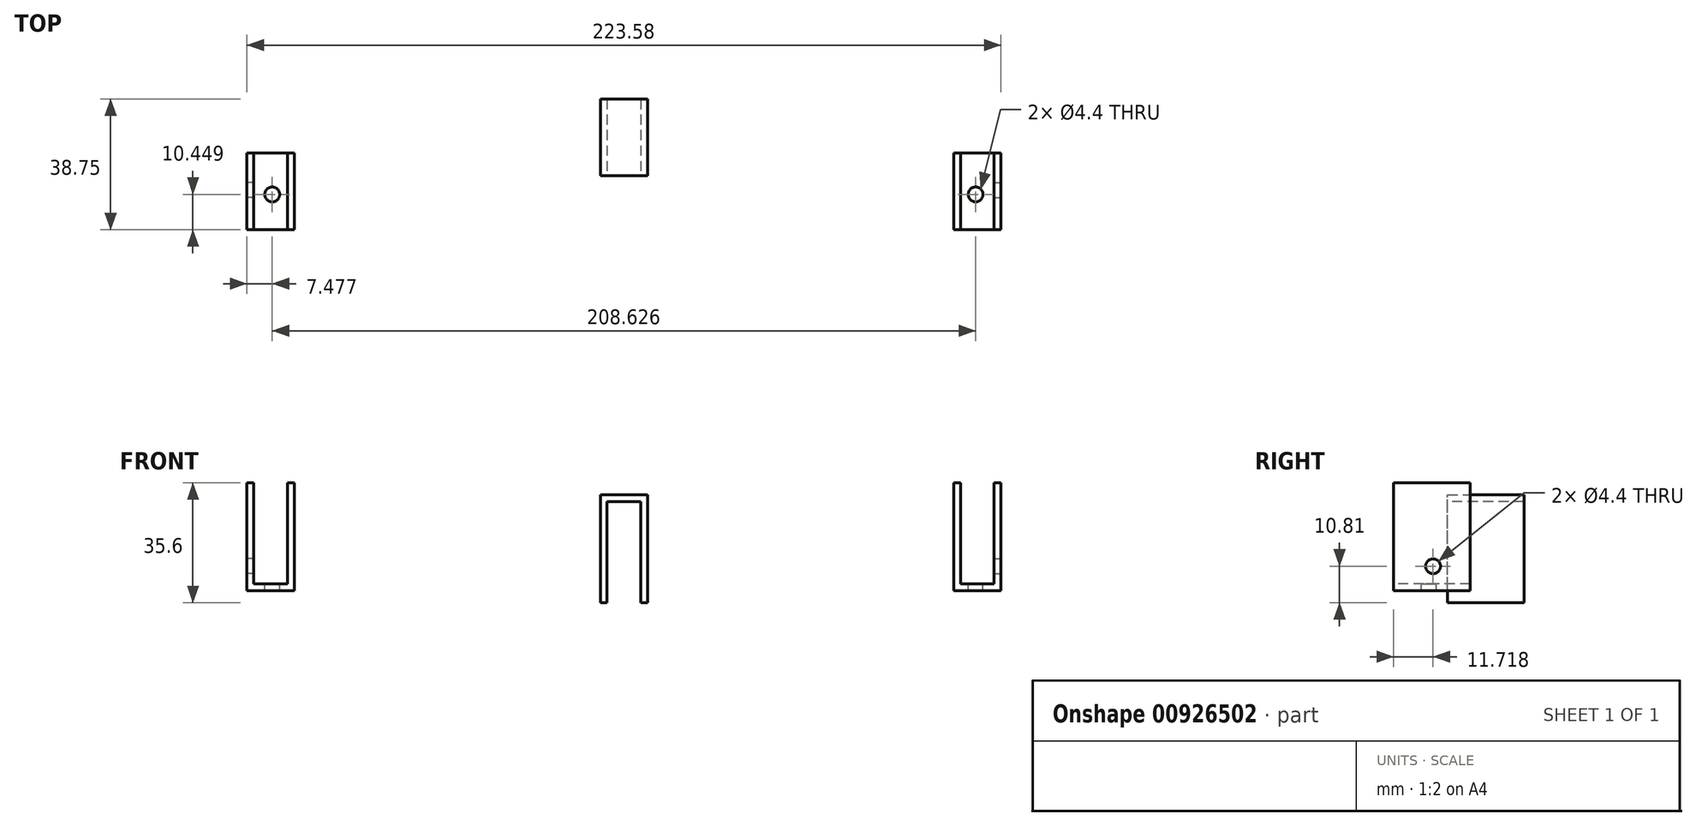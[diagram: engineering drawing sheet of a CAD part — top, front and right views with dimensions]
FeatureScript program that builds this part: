
annotation { "Feature Type Name" : "Feature", "Feature Type Description" : "" }
export const myFeature = defineFeature(function(context is Context, id is Id, definition is map)
    precondition{}
    {
        {
            var Q0;
            Q0=qCreatedBy(id+"FDib9sGqoO0YXEu_1.planeOp",FACE);
            var Q1;
            Q1=qCreatedBy(makeId("Front.planeOp"),FACE);
            var Q2;
            Q2=makeQuery(id+"FSaKtVyOSRUwnGU_0.opExtrude","SWEPT_FACE",FACE,{"disambiguationData":[OSD([sQuery(id+"FrPxosmD42h2brX_0.wireOp",EDGE,"dLfLj8vu-IHSN-0c34-1Y5T-tfJKqT0q3hT1.top")])]});
            var Q3;
            Q3=makeQuery(id+"FSaKtVyOSRUwnGU_0.opExtrude","SWEPT_FACE",FACE,{"disambiguationData":[OSD([sQuery(id+"FrPxosmD42h2brX_0.wireOp",EDGE,"dLfLj8vu-IHSN-0c34-1Y5T-tfJKqT0q3hT1.right")])]});
            var sketch = newSketch(context, id + "F0", { "sketchPlane" : qUnion([Q0, Q1, Q2, Q3])});
            skSolve(sketch);
        }
        {
            var Q0;
            Q0=qCreatedBy(makeId("Top.planeOp"),FACE);
            var sketch = newSketch(context, id + "F1", { "sketchPlane" : qUnion([Q0])});
            skLineSegment(sketch, "E0.bottom", {"start": v(97.8, -44.35) * mm, "end": v(111.8, -44.35) * mm});
            skLineSegment(sketch, "E0.top", {"start": v(97.8, -21.6) * mm, "end": v(111.8, -21.6) * mm});
            skLineSegment(sketch, "E0.left", {"start": v(97.8, -44.35) * mm, "end": v(97.8, -21.6) * mm});
            skLineSegment(sketch, "E0.right", {"start": v(111.8, -44.35) * mm, "end": v(111.8, -21.6) * mm});
            skSolve(sketch);
        }
        {
            var Q0;
            Q0 = qSketchRegion(id + "F1", true);
            extrude(context, id + "F2", {"entities" : qUnion([Q0]), "depth" : 2 * mm, "offsetDistance" : 25.4 * mm});
        }
        {
            var Q0;
            Q0=makeQuery(id+"F2.opExtrude","CAP_FACE",FACE,{"disambiguationData":[OSD([sQuery(id+"F1.wireOp",EDGE,"E0.bottom"),sQuery(id+"F1.wireOp",EDGE,"E0.top"),sQuery(id+"F1.wireOp",EDGE,"E0.left"),sQuery(id+"F1.wireOp",EDGE,"E0.right")])],"isStart":false});
            var sketch = newSketch(context, id + "F3", { "sketchPlane" : qUnion([Q0])});
            skLineSegment(sketch, "E1.bottom", {"start": v(97.8, -21.6) * mm, "end": v(99.8, -21.6) * mm});
            skLineSegment(sketch, "E1.top", {"start": v(97.8, -44.35) * mm, "end": v(99.8, -44.35) * mm});
            skLineSegment(sketch, "E1.left", {"start": v(97.8, -21.6) * mm, "end": v(97.8, -44.35) * mm});
            skLineSegment(sketch, "E1.right", {"start": v(99.8, -21.6) * mm, "end": v(99.8, -44.35) * mm});
            skLineSegment(sketch, "E2.bottom", {"start": v(111.8, -21.6) * mm, "end": v(109.8, -21.6) * mm});
            skLineSegment(sketch, "E2.top", {"start": v(111.8, -44.35) * mm, "end": v(109.8, -44.35) * mm});
            skLineSegment(sketch, "E2.left", {"start": v(111.8, -21.6) * mm, "end": v(111.8, -44.35) * mm});
            skLineSegment(sketch, "E2.right", {"start": v(109.8, -21.6) * mm, "end": v(109.8, -44.35) * mm});
            skSolve(sketch);
        }
        {
            var Q0;
            Q0 = qSketchRegion(id + "F3", true);
            extrude(context, id + "F4", {"entities" : qUnion([Q0]), "operationType" : NewBodyOperationType.ADD, "depth" : 30 * mm, "offsetDistance" : 25.4 * mm});
        }
        {
            var Q0;
            Q0=makeQuery(id+"F4.boolean.opBoolean","MERGE",FACE,{"derivedFrom":[makeQuery(id+"F2.opExtrude","SWEPT_FACE",FACE,{"disambiguationData":[OSD([sQuery(id+"F1.wireOp",EDGE,"E0.right")])]}),makeQuery(id+"F4.opExtrude","SWEPT_FACE",FACE,{"disambiguationData":[OSD([sQuery(id+"F3.wireOp",EDGE,"E2.left")])]})]});
            var sketch = newSketch(context, id + "F5", { "sketchPlane" : qUnion([Q0])});
            skCircle(sketch, "E3", {"center": v(-32.63, 7.2) * mm, "radius": 2.2 * mm});
            skSolve(sketch);
        }
        {
            var Q0;
            Q0 = qSketchRegion(id + "F5", true);
            extrude(context, id + "F6", {"entities" : qUnion([Q0]), "operationType" : NewBodyOperationType.REMOVE, "endBound" : BoundingType.UP_TO_NEXT, "oppositeDirection" : true, "depth" : 25.4 * mm, "offsetDistance" : 25.4 * mm});
        }
        {
            var Q0;
            Q0=makeQuery(id+"F2.opExtrude","CAP_FACE",FACE,{"disambiguationData":[OSD([sQuery(id+"F1.wireOp",EDGE,"E0.bottom"),sQuery(id+"F1.wireOp",EDGE,"E0.top"),sQuery(id+"F1.wireOp",EDGE,"E0.left"),sQuery(id+"F1.wireOp",EDGE,"E0.right")])],"isStart":false});
            var sketch = newSketch(context, id + "F7", { "sketchPlane" : qUnion([Q0])});
            skCircle(sketch, "E4", {"center": v(104.31, -33.9) * mm, "radius": 2.2 * mm});
            skSolve(sketch);
        }
        {
            var Q0;
            Q0 = qSketchRegion(id + "F7", true);
            extrude(context, id + "F8", {"entities" : qUnion([Q0]), "operationType" : NewBodyOperationType.REMOVE, "endBound" : BoundingType.UP_TO_NEXT, "oppositeDirection" : true, "depth" : 25.4 * mm, "offsetDistance" : 25.4 * mm});
        }
        {
            var Q0;
            Q0=makeQuery(id+"F2.opExtrude","SWEPT_BODY",BODY,{"disambiguationData":[OSD([sQuery(id+"F1.wireOp",EDGE,"E0.bottom"),sQuery(id+"F1.wireOp",EDGE,"E0.top"),sQuery(id+"F1.wireOp",EDGE,"E0.left"),sQuery(id+"F1.wireOp",EDGE,"E0.right")])]});
            var Q1;
            Q1=qCreatedBy(makeId("Right.planeOp"),FACE);
            mirror(context, id + "F9", {"entities" : qUnion([Q0]), "mirrorPlane" : qUnion([Q1])});
        }
        {
            var Q0;
            Q0=makeQuery(id+"F9.opPattern","COPY",BODY,{"derivedFrom":makeQuery(id+"F2.opExtrude","SWEPT_BODY",BODY,{"disambiguationData":[OSD([sQuery(id+"F1.wireOp",EDGE,"E0.bottom"),sQuery(id+"F1.wireOp",EDGE,"E0.top"),sQuery(id+"F1.wireOp",EDGE,"E0.left"),sQuery(id+"F1.wireOp",EDGE,"E0.right")])]}),"instanceName":"1"});
            var Q1;
            Q1=makeQuery(id+"F9.opPattern","COPY",EDGE,{"derivedFrom":makeQuery(id+"F2.opExtrude","CAP_EDGE",EDGE,{"disambiguationData":[OSD([sQuery(id+"F1.wireOp",EDGE,"E0.left")])],"isStart":true}),"instanceName":"1"});
            transform(context, id + "F10", {"entities" : qUnion([Q0]), "transformType" : TransformType.ROTATION, "transformAxis" : qUnion([Q1]), "angle" : 180 * degree, "makeCopy" : true});
        }
        {
            var Q0;
            Q0=makeQuery(id+"F10.opPattern","COPY",BODY,{"derivedFrom":makeQuery(id+"F9.opPattern","COPY",BODY,{"derivedFrom":makeQuery(id+"F2.opExtrude","SWEPT_BODY",BODY,{"disambiguationData":[OSD([sQuery(id+"F1.wireOp",EDGE,"E0.bottom"),sQuery(id+"F1.wireOp",EDGE,"E0.top"),sQuery(id+"F1.wireOp",EDGE,"E0.left"),sQuery(id+"F1.wireOp",EDGE,"E0.right")])]}),"instanceName":"1"}),"instanceName":"1"});
            transform(context, id + "F11", {"entities" : qUnion([Q0]), "transformType" : TransformType.TRANSLATION_3D, "dx" : 90.8 * mm, "dy" : 16 * mm, "dz" : 28.4 * mm, "makeCopy" : false});
        }
        {
            var Q0;
            Q0=makeQuery(id+"F10.opPattern","COPY",FACE,{"derivedFrom":makeQuery(id+"F9.opPattern","COPY",FACE,{"derivedFrom":makeQuery(id+"F2.opExtrude","CAP_FACE",FACE,{"disambiguationData":[OSD([sQuery(id+"F1.wireOp",EDGE,"E0.bottom"),sQuery(id+"F1.wireOp",EDGE,"E0.top"),sQuery(id+"F1.wireOp",EDGE,"E0.left"),sQuery(id+"F1.wireOp",EDGE,"E0.right")])],"isStart":true}),"instanceName":"1"}),"instanceName":"1"});
            cPlane(context, id + "F12", {"entities" : qUnion([Q0]), "cplaneType" : CPlaneType.OFFSET, "offset" : 0 * mm, "width" : 150 * mm, "height" : 150 * mm});
        }
        {
            var Q0;
            Q0=qCreatedBy(id+"F12.planeOp",FACE);
            var sketch = newSketch(context, id + "F13", { "sketchPlane" : qUnion([Q0])});
            skLineSegment(sketch, "E5.bottom", {"start": v(-3.68, -22.94) * mm, "end": v(3.47, -22.94) * mm});
            skLineSegment(sketch, "E5.top", {"start": v(-3.68, -12.56) * mm, "end": v(3.47, -12.56) * mm});
            skLineSegment(sketch, "E5.left", {"start": v(-3.68, -22.94) * mm, "end": v(-3.68, -12.56) * mm});
            skLineSegment(sketch, "E5.right", {"start": v(3.47, -22.94) * mm, "end": v(3.47, -12.56) * mm});
            skSolve(sketch);
        }
        {
            var Q0;
            Q0 = qSketchRegion(id + "F13", true);
            var Q1;
            Q1=makeQuery(id+"F10.opPattern","COPY",FACE,{"derivedFrom":makeQuery(id+"F9.opPattern","COPY",FACE,{"derivedFrom":makeQuery(id+"F2.opExtrude","CAP_FACE",FACE,{"disambiguationData":[OSD([sQuery(id+"F1.wireOp",EDGE,"E0.bottom"),sQuery(id+"F1.wireOp",EDGE,"E0.top"),sQuery(id+"F1.wireOp",EDGE,"E0.left"),sQuery(id+"F1.wireOp",EDGE,"E0.right")])],"isStart":false}),"instanceName":"1"}),"instanceName":"1"});
            extrude(context, id + "F14", {"entities" : qUnion([Q0]), "operationType" : NewBodyOperationType.ADD, "endBound" : BoundingType.UP_TO_SURFACE, "oppositeDirection" : true, "depth" : 25 * mm, "endBoundEntityFace" : qUnion([Q1]), "offsetDistance" : 25 * mm});
        }
        {
            var Q0;
            Q0=makeQuery(id+"F10.opPattern","COPY",FACE,{"derivedFrom":makeQuery(id+"F9.opPattern","COPY",FACE,{"derivedFrom":makeQuery(id+"F4.boolean.opBoolean","MERGE",FACE,{"derivedFrom":[makeQuery(id+"F2.opExtrude","SWEPT_FACE",FACE,{"disambiguationData":[OSD([sQuery(id+"F1.wireOp",EDGE,"E0.right")])]}),makeQuery(id+"F4.opExtrude","SWEPT_FACE",FACE,{"disambiguationData":[OSD([sQuery(id+"F3.wireOp",EDGE,"E2.left")])]})]}),"instanceName":"1"}),"instanceName":"1"});
            cPlane(context, id + "F15", {"entities" : qUnion([Q0]), "cplaneType" : CPlaneType.OFFSET, "offset" : 0 * mm, "width" : 150 * mm, "height" : 150 * mm});
        }
        {
            var Q0;
            Q0=qCreatedBy(id+"F15.planeOp",FACE);
            var sketch = newSketch(context, id + "F16", { "sketchPlane" : qUnion([Q0])});
            skLineSegment(sketch, "E6.bottom", {"start": v(-25.66, 25.5) * mm, "end": v(-6.98, 25.5) * mm});
            skLineSegment(sketch, "E6.top", {"start": v(-25.66, 16.34) * mm, "end": v(-6.98, 16.34) * mm});
            skLineSegment(sketch, "E6.left", {"start": v(-25.66, 25.5) * mm, "end": v(-25.66, 16.34) * mm});
            skLineSegment(sketch, "E6.right", {"start": v(-6.98, 25.5) * mm, "end": v(-6.98, 16.34) * mm});
            skSolve(sketch);
        }
        {
            var Q0;
            Q0=makeQuery(id+"F16.imprint","IMPRINT",FACE,{"disambiguationData":[TD([[makeQuery(id+"F16.imprint","IMPRINT",EDGE,{"derivedFrom":sQuery(id+"F16.wireOp",EDGE,"E6.bottom")}),-1.0]])]});
            var Q1;
            Q1=makeQuery(id+"F10.opPattern","COPY",FACE,{"derivedFrom":makeQuery(id+"F9.opPattern","COPY",FACE,{"derivedFrom":makeQuery(id+"F4.opExtrude","SWEPT_FACE",FACE,{"disambiguationData":[OSD([sQuery(id+"F3.wireOp",EDGE,"E2.right")])]}),"instanceName":"1"}),"instanceName":"1"});
            extrude(context, id + "F17", {"entities" : qUnion([Q0]), "operationType" : NewBodyOperationType.ADD, "endBound" : BoundingType.UP_TO_SURFACE, "oppositeDirection" : true, "depth" : 25 * mm, "endBoundEntityFace" : qUnion([Q1]), "offsetDistance" : 25 * mm});
        }
    });
